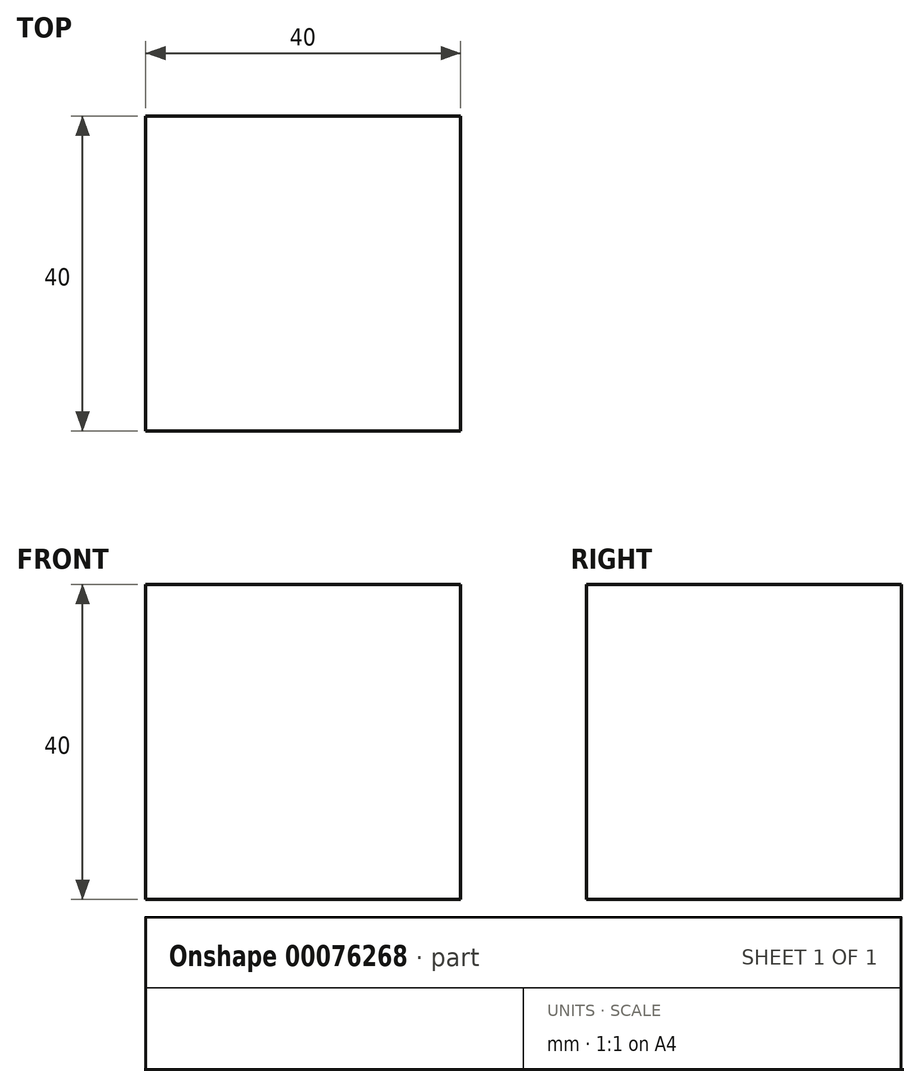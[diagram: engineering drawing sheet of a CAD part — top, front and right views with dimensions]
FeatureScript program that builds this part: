
annotation { "Feature Type Name" : "Feature", "Feature Type Description" : "" }
export const myFeature = defineFeature(function(context is Context, id is Id, definition is map)
    precondition{}
    {
        {
            var Q0;
            Q0=qCreatedBy(makeId("Front.planeOp"),FACE);
            var sketch = newSketch(context, id + "F0", { "sketchPlane" : qUnion([Q0])});
            skLineSegment(sketch, "E0.bottom", {"start": v(0, 0) * mm, "end": v(40, 0) * mm});
            skLineSegment(sketch, "E0.top", {"start": v(0, 40) * mm, "end": v(40, 40) * mm});
            skLineSegment(sketch, "E0.left", {"start": v(0, 0) * mm, "end": v(0, 40) * mm});
            skLineSegment(sketch, "E0.right", {"start": v(40, 0) * mm, "end": v(40, 40) * mm});
            skSolve(sketch);
        }
        {
            var Q0;
            Q0 = qSketchRegion(id + "F0", true);
            var Q1;
            Q1=makeQuery(id+"F0.imprint","IMPRINT",FACE,{"disambiguationData":[TD([[makeQuery(id+"F0.imprint","IMPRINT",EDGE,{"derivedFrom":sQuery(id+"F0.wireOp",EDGE,"E0.bottom")}),1.0]])]});
            extrude(context, id + "F1", {"entities" : qUnion([Q0, Q1]), "depth" : 40 * mm});
        }
    });
